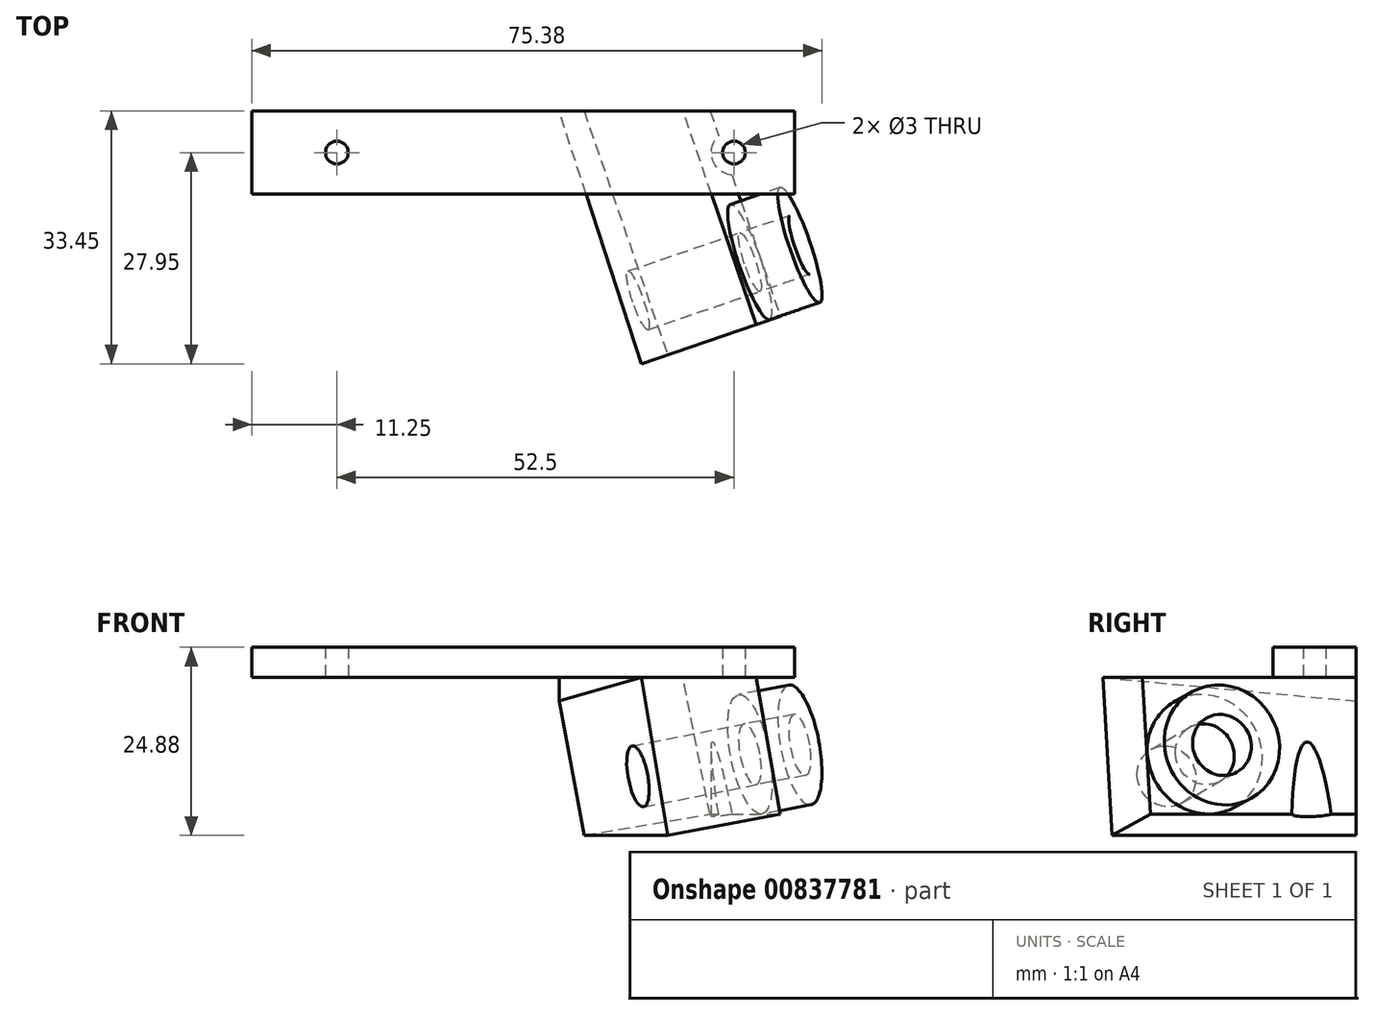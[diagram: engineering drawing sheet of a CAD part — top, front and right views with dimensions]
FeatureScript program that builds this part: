
annotation { "Feature Type Name" : "Feature", "Feature Type Description" : "" }
export const myFeature = defineFeature(function(context is Context, id is Id, definition is map)
    precondition{}
    {
        {
            var Q0;
            Q0=qCreatedBy(makeId("Top.planeOp"),FACE);
            var sketch = newSketch(context, id + "F0", { "sketchPlane" : qUnion([Q0])});
            skLineSegment(sketch, "E0.bottom", {"start": v(37.5, 5.5) * mm, "end": v(-37.5, 5.5) * mm});
            skLineSegment(sketch, "E0.top", {"start": v(37.5, -5.5) * mm, "end": v(-37.5, -5.5) * mm});
            skLineSegment(sketch, "E0.left", {"start": v(37.5, 5.5) * mm, "end": v(37.5, -5.5) * mm});
            skLineSegment(sketch, "E0.right", {"start": v(-37.5, 5.5) * mm, "end": v(-37.5, -5.5) * mm});
            skPoint(sketch, "E0.middle", {"position": v(0, 0) * mm});
            skLineSegment(sketch, "E1", {"start": v(0, 0) * mm, "end": v(-15, 0) * mm, "construction": true});
            skLineSegment(sketch, "E2", {"start": v(0, 0) * mm, "end": v(15, 0) * mm, "construction": true});
            skLineSegment(sketch, "E3", {"start": v(-15, 0) * mm, "end": v(-26.25, 0) * mm, "construction": true});
            skLineSegment(sketch, "E4", {"start": v(15, 0) * mm, "end": v(26.25, 0) * mm, "construction": true});
            skCircle(sketch, "E5", {"center": v(-26.25, 0) * mm, "radius": 1.5 * mm});
            skCircle(sketch, "E6", {"center": v(26.25, 0) * mm, "radius": 1.5 * mm});
            skLineSegment(sketch, "E7", {"start": v(-37.5, 5.5) * mm, "end": v(-43.1, -5.5) * mm, "construction": true});
            skLineSegment(sketch, "E8", {"start": v(-37.5, -5.5) * mm, "end": v(-43.1, -5.5) * mm, "construction": true});
            skLineSegment(sketch, "E9", {"start": v(77.8, 6.5) * mm, "end": v(-101.6, -33.5) * mm, "construction": true});
            skLineSegment(sketch, "E10", {"start": v(-101.6, -33.5) * mm, "end": v(-99.87, -41.3) * mm, "construction": true});
            skLineSegment(sketch, "E11", {"start": v(-99.87, -41.3) * mm, "end": v(79.55, -1.3) * mm, "construction": true});
            skLineSegment(sketch, "E12", {"start": v(77.8, 6.5) * mm, "end": v(79.55, -1.3) * mm, "construction": true});
            skLineSegment(sketch, "E13", {"start": v(24.75, 0) * mm, "end": v(20.75, 0) * mm, "construction": true});
            skLineSegment(sketch, "E14", {"start": v(20.75, 0) * mm, "end": v(19.52, 5.5) * mm, "construction": true});
            skLineSegment(sketch, "E15", {"start": v(20.75, 0) * mm, "end": v(5.13, -3.48) * mm, "construction": true});
            skLineSegment(sketch, "E16", {"start": v(5.13, -3.48) * mm, "end": v(3.13, 5.5) * mm, "construction": true});
            skLineSegment(sketch, "E17", {"start": v(37.5, 5.5) * mm, "end": v(37.5, 9.6) * mm});
            skLineSegment(sketch, "E18", {"start": v(37.5, 9.6) * mm, "end": v(-37.23, 9.6) * mm});
            skLineSegment(sketch, "E19", {"start": v(-37.23, 9.6) * mm, "end": v(-37.5, 5.5) * mm});
            skCircle(sketch, "E20", {"center": v(26.25, 0) * mm, "radius": 3 * mm});
            skLineSegment(sketch, "E21", {"start": v(29.25, 0) * mm, "end": v(34.25, 0) * mm, "construction": true});
            skLineSegment(sketch, "E22", {"start": v(34.25, 0) * mm, "end": v(34.25, 9.6) * mm, "construction": true});
            skLineSegment(sketch, "E23", {"start": v(34.25, 0) * mm, "end": v(34.25, -5.5) * mm, "construction": true});
            skLineSegment(sketch, "E24", {"start": v(-27.75, 0) * mm, "end": v(-32.75, 0) * mm, "construction": true});
            skLineSegment(sketch, "E25", {"start": v(-32.75, 0) * mm, "end": v(-32.75, 9.6) * mm, "construction": true});
            skLineSegment(sketch, "E26", {"start": v(-32.75, 0) * mm, "end": v(-32.75, -5.5) * mm, "construction": true});
            skLineSegment(sketch, "E27", {"start": v(34.25, 5.5) * mm, "end": v(34.25, -5.5) * mm});
            skLineSegment(sketch, "E28", {"start": v(-32.75, 5.5) * mm, "end": v(-32.75, -5.5) * mm});
            skLineSegment(sketch, "E29", {"start": v(18.44, -26.4) * mm, "end": v(17.57, -22.5) * mm, "construction": true});
            skLineSegment(sketch, "E30", {"start": v(17.57, -22.5) * mm, "end": v(79.55, -1.3) * mm, "construction": true});
            skLineSegment(sketch, "E31", {"start": v(17.57, -22.5) * mm, "end": v(-94.74, -60.9) * mm, "construction": true});
            skLineSegment(sketch, "E32", {"start": v(-94.74, -60.9) * mm, "end": v(-97.4, -53.14) * mm, "construction": true});
            skLineSegment(sketch, "E33", {"start": v(-97.4, -53.14) * mm, "end": v(75.6, 6.02) * mm, "construction": true});
            skLineSegment(sketch, "E34", {"start": v(75.6, 6.02) * mm, "end": v(79.55, -1.3) * mm, "construction": true});
            skLineSegment(sketch, "E35", {"start": v(19.52, 5.5) * mm, "end": v(27.9, -18.96) * mm});
            skLineSegment(sketch, "E36", {"start": v(27.9, -18.96) * mm, "end": v(12.75, -24.14) * mm});
            skLineSegment(sketch, "E37", {"start": v(12.75, -24.14) * mm, "end": v(3.13, 5.5) * mm});
            skLineSegment(sketch, "E38", {"start": v(12.75, -24.14) * mm, "end": v(13.99, -27.95) * mm});
            skLineSegment(sketch, "E39", {"start": v(27.9, -18.96) * mm, "end": v(29.18, -22.75) * mm});
            skLineSegment(sketch, "E40", {"start": v(29.18, -22.75) * mm, "end": v(13.99, -27.95) * mm});
            skSolve(sketch);
        }
        {
            var Q0;
            {var subQ5=sQuery(id+"F0.wireOp",EDGE,"iJbbgQNM-ICqB-zzGx-AGRb-dF4PoK6hcDrh");Q0=makeQuery(id+"F0.imprint","IMPRINT",FACE,{"disambiguationData":[TD([[makeQuery(id+"F0.imprint","IMPRINT",EDGE,{"derivedFrom":subQ5}),-1.0]])]});}
            var Q1;
            {var subQ0=sQuery(id+"F0.wireOp",EDGE,"0qUmDRuC-nkU8-DhKB-LSF8-CPz10Ho4At5o");var subQ1=sQuery(id+"F0.wireOp",EDGE,"E0.bottom");var subQ2=makeQuery(id+"F0.imprint","INTERSECT",VERTEX,{"derivedFrom":[subQ1,subQ0]});Q1=makeQuery(id+"F0.imprint","IMPRINT",FACE,{"disambiguationData":[TD([[makeQuery(id+"F0.imprint","IMPRINT",EDGE,{"disambiguationData":[TD([[subQ2,-1.0]])],"derivedFrom":subQ1}),1.0]])]});}
            var Q2;
            Q2=makeQuery(id+"F0.imprint","IMPRINT",FACE,{"disambiguationData":[TD([[makeQuery(id+"F0.imprint","IMPRINT",EDGE,{"derivedFrom":sQuery(id+"F0.wireOp",EDGE,"E6")}),-1.0]])]});
            var Q3;
            Q3=makeQuery(id+"F0.imprint","IMPRINT",FACE,{"disambiguationData":[TD([[makeQuery(id+"F0.imprint","IMPRINT",EDGE,{"derivedFrom":sQuery(id+"F0.wireOp",EDGE,"E20")}),-1.0]])]});
            var Q4;
            Q4=makeQuery(id+"F0.imprint","IMPRINT",FACE,{"disambiguationData":[TD([[makeQuery(id+"F0.imprint","IMPRINT",EDGE,{"derivedFrom":sQuery(id+"F0.wireOp",EDGE,"E5")}),-1.0]])]});
            extrude(context, id + "F1", {"entities" : qUnion([Q0, Q1, Q2, Q3, Q4]), "depth" : 4 * mm, "offsetDistance" : 25 * mm});
        }
        {
            var Q0;
            {var subQ0=sQuery(id+"F0.wireOp",EDGE,"E35");var subQ1=sQuery(id+"F0.wireOp",EDGE,"E0.bottom");var subQ2=makeQuery(id+"F0.imprint","INTERSECT",VERTEX,{"derivedFrom":[subQ1,subQ0]});Q0=makeQuery(id+"F0.imprint","IMPRINT",FACE,{"disambiguationData":[TD([[makeQuery(id+"F0.imprint","IMPRINT",EDGE,{"disambiguationData":[TD([[subQ2,-1.0]])],"derivedFrom":subQ1}),1.0]])]});}
            var Q1;
            {var subQ5=sQuery(id+"F0.wireOp",EDGE,"E36");Q1=makeQuery(id+"F0.imprint","IMPRINT",FACE,{"disambiguationData":[TD([[makeQuery(id+"F0.imprint","IMPRINT",EDGE,{"derivedFrom":subQ5}),-1.0]])]});}
            var Q2;
            Q2=makeQuery(id+"F0.imprint","IMPRINT",FACE,{"disambiguationData":[TD([[makeQuery(id+"F0.imprint","IMPRINT",EDGE,{"derivedFrom":sQuery(id+"F0.wireOp",EDGE,"E36")}),1.0]])]});
            extrude(context, id + "F2", {"entities" : qUnion([Q0, Q1, Q2]), "operationType" : NewBodyOperationType.ADD, "oppositeDirection" : true, "depth" : 21.2 * mm, "offsetDistance" : 25 * mm});
        }
        {
            var Q0;
            Q0=makeQuery(id+"F2.opExtrude","SWEPT_FACE",FACE,{"disambiguationData":[OSD([sQuery(id+"F0.wireOp",EDGE,"E40")])]});
            var sketch = newSketch(context, id + "F3", { "sketchPlane" : qUnion([Q0])});
            skLineSegment(sketch, "E41", {"start": v(4.2, 0) * mm, "end": v(7.87, -20.88) * mm});
            skLineSegment(sketch, "E42", {"start": v(7.87, -20.88) * mm, "end": v(23.63, -18.1) * mm});
            skLineSegment(sketch, "E43", {"start": v(23.63, -18.1) * mm, "end": v(20.25, 0) * mm});
            skSolve(sketch);
        }
        {
            var Q0;
            {var subQ3=sQuery(id+"F3.wireOp",EDGE,"E41");Q0=makeQuery(id+"F3.imprint","IMPRINT",FACE,{"disambiguationData":[TD([[makeQuery(id+"F3.imprint","IMPRINT",EDGE,{"derivedFrom":subQ3}),-1.0]])]});}
            extrude(context, id + "F4", {"entities" : qUnion([Q0]), "operationType" : NewBodyOperationType.REMOVE, "oppositeDirection" : true, "depth" : 40 * mm, "offsetDistance" : 25 * mm});
        }
        {
            var Q0;
            {var subQ0=sQuery(id+"F3.wireOp",EDGE,"E43");Q0=makeQuery(id+"F3.imprint","IMPRINT",FACE,{"disambiguationData":[TD([[makeQuery(id+"F3.imprint","IMPRINT",EDGE,{"derivedFrom":subQ0}),1.0]])]});}
            extrude(context, id + "F5", {"entities" : qUnion([Q0]), "operationType" : NewBodyOperationType.ADD, "oppositeDirection" : true, "depth" : 32 * mm, "offsetDistance" : 25 * mm});
        }
        {
            var Q0;
            {var subQ3=sQuery(id+"F0.wireOp",EDGE,"E17");Q0=makeQuery(id+"F0.imprint","IMPRINT",FACE,{"disambiguationData":[TD([[makeQuery(id+"F0.imprint","IMPRINT",EDGE,{"derivedFrom":subQ3}),1.0]])]});}
            extrude(context, id + "F6", {"entities" : qUnion([Q0]), "operationType" : NewBodyOperationType.REMOVE, "oppositeDirection" : true, "depth" : 25 * mm, "offsetDistance" : 25 * mm});
        }
        {
            var Q0;
            Q0=makeQuery(id+"F4.boolean.opBoolean","COPY",FACE,{"derivedFrom":makeQuery(id+"F4.opExtrude","SWEPT_FACE",FACE,{"disambiguationData":[OSD([sQuery(id+"F3.wireOp",EDGE,"E41")])]})});
            var sketch = newSketch(context, id + "F7", { "sketchPlane" : qUnion([Q0])});
            skLineSegment(sketch, "E44", {"start": v(-4.41, -15.17) * mm, "end": v(30.12, -15.17) * mm});
            skLineSegment(sketch, "E45", {"start": v(30.12, -15.17) * mm, "end": v(22.02, -15.17) * mm});
            skLineSegment(sketch, "E46", {"start": v(22.02, -15.17) * mm, "end": v(22.02, -23.27) * mm});
            skCircle(sketch, "E47", {"center": v(22.02, -15.17) * mm, "radius": 8.05 * mm});
            skCircle(sketch, "E48", {"center": v(22.02, -15.17) * mm, "radius": 4.1 * mm});
            skSolve(sketch);
        }
        {
            var Q0;
            {var subQ0=sQuery(id+"F7.wireOp",EDGE,"E47");var subQ1=sQuery(id+"F7.wireOp",EDGE,"E44");var subQ2=makeQuery(id+"F7.imprint","INTERSECT",VERTEX,{"disambiguationData":[OD(0.0)],"derivedFrom":[subQ1,subQ0]});var subQ3=sQuery(id+"F7.wireOp",EDGE,"E48");var subQ5=makeQuery(id+"F7.imprint","IMPRINT",EDGE,{"disambiguationData":[TD([[subQ2,-1.0]])],"derivedFrom":subQ1});var subQ10=makeQuery(id+"F7.imprint","INTERSECT",VERTEX,{"disambiguationData":[OD(0.0)],"derivedFrom":[subQ1,subQ3]});var subQ12=makeQuery(id+"F7.imprint","IMPRINT",EDGE,{"disambiguationData":[TD([[subQ10,-1.0]])],"derivedFrom":subQ1});Q0=qUnion([makeQuery(id+"F7.imprint","IMPRINT",FACE,{"disambiguationData":[TD([[subQ12,1.0]])]}),makeQuery(id+"F7.imprint","IMPRINT",FACE,{"disambiguationData":[TD([[subQ12,-1.0]])]}),makeQuery(id+"F7.imprint","IMPRINT",FACE,{"disambiguationData":[TD([[subQ5,-1.0]])]})]);}
            extrude(context, id + "F8", {"entities" : qUnion([Q0]), "operationType" : NewBodyOperationType.ADD, "oppositeDirection" : true, "depth" : 23 * mm, "offsetDistance" : 25 * mm});
        }
        {
            var Q0;
            Q0=makeQuery(id+"F8.boolean.opBoolean","SPLIT",FACE,{"disambiguationData":[TD([makeQuery(id+"F8.opExtrude","SWEPT_FACE",FACE,{"disambiguationData":[OSD([sQuery(id+"F7.wireOp",EDGE,"E48")])]})])],"derivedFrom":makeQuery(id+"F5.opExtrude","SWEPT_FACE",FACE,{"disambiguationData":[OSD([sQuery(id+"F3.wireOp",EDGE,"E43")])]})});
            extrude(context, id + "F9", {"entities" : qUnion([Q0]), "operationType" : NewBodyOperationType.REMOVE, "oppositeDirection" : true, "depth" : 25 * mm, "offsetDistance" : 25 * mm});
        }
        {
            var Q0;
            Q0=makeQuery(id+"F0.imprint","IMPRINT",FACE,{"disambiguationData":[TD([[makeQuery(id+"F0.imprint","IMPRINT",EDGE,{"derivedFrom":sQuery(id+"F0.wireOp",EDGE,"E6")}),-1.0]])]});
            var Q1;
            Q1=makeQuery(id+"F0.imprint","IMPRINT",FACE,{"disambiguationData":[TD([[makeQuery(id+"F0.imprint","IMPRINT",EDGE,{"derivedFrom":sQuery(id+"F0.wireOp",EDGE,"E6")}),1.0]])]});
            extrude(context, id + "F10", {"entities" : qUnion([Q0, Q1]), "operationType" : NewBodyOperationType.REMOVE, "oppositeDirection" : true, "depth" : 25 * mm, "offsetDistance" : 25 * mm});
        }
    });
